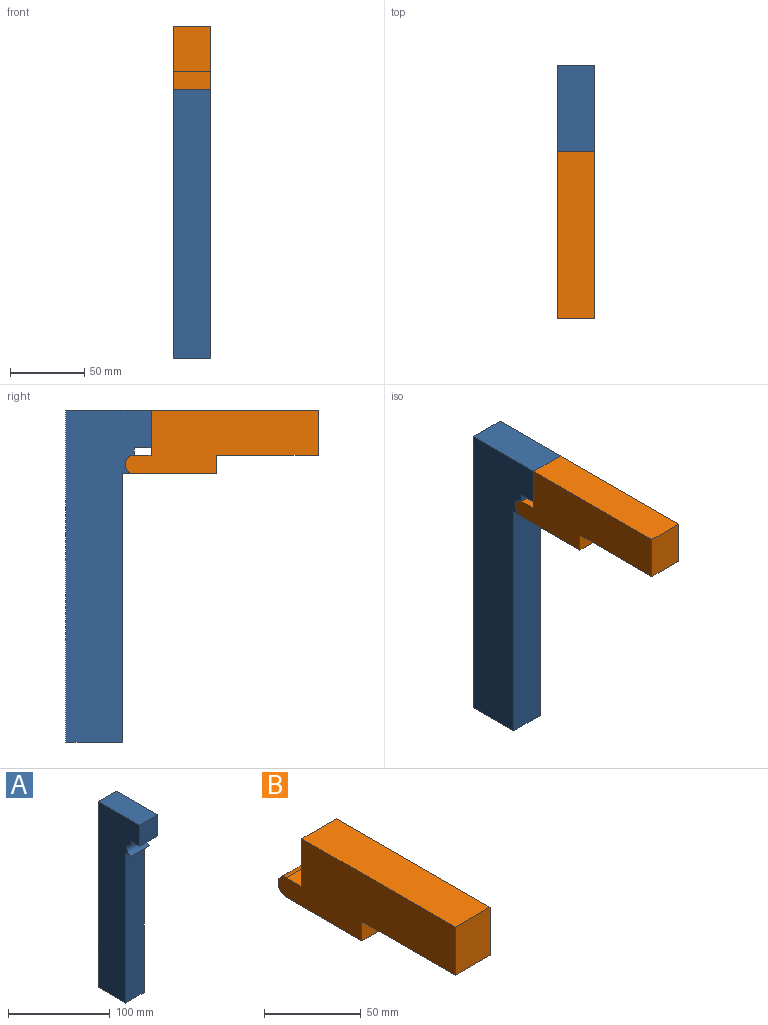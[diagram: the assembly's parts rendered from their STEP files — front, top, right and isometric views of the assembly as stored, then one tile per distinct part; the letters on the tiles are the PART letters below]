
ASSEMBLY  parts=2 mates=1
PART A: 11 faces, bbox 25.4x57.3x223 mm
  f0: plane 25.4x11.35mm, normal (0,0,-1), area 288.3mm2, adj f1,f8,f9,f10
  f1: plane 25.4x5.08mm, normal (0,-1,0), area 129mm2, adj f0,f2,f9,f10
  f2: cylinder r=6.14mm len=25.4mm, axis (-1,0,0), area 490.1mm2, adj f1,f3,f9,f10
  f3: plane 25.4x7.7mm, normal (0,0,-1), area 195.6mm2, adj f2,f4,f9,f10
  f4: plane 180.26x25.4mm, normal (0,-1,0), area 4578.6mm2, adj f3,f5,f9,f10
  f5: plane 38.21x25.4mm, normal (0,0,-1), area 970.4mm2, adj f4,f6,f9,f10
  f6: plane 223.02x25.4mm, normal (0,1,0), area 5664.8mm2, adj f5,f7,f9,f10
  f7: plane 57.26x25.4mm, normal (0,0,1), area 1454.3mm2, adj f6,f8,f9,f10
  f8: plane 25.4x25.4mm, normal (0,-1,0), area 645.2mm2, adj f0,f7,f9,f10
  f9: plane 223.02x57.26mm, normal (1,0,0), area 9078.9mm2, adj f0,f1,f2,f3,f4,f5,f6,f7
  f10: plane 223.02x57.26mm, normal (-1,0,0), area 9078.9mm2, adj f0,f1,f2,f3,f4,f5,f6,f7
PART B: 10 faces, bbox 25.4x129.7x42.8 mm
  f0: plane 68.31x25.4mm, normal (0,0,-1), area 1735.2mm2, adj f1,f7,f8,f9
  f1: plane 25.4x12.28mm, normal (0,-1,0), area 312mm2, adj f0,f2,f8,f9
  f2: plane 55.28x25.4mm, normal (0,0,-1), area 1404mm2, adj f1,f3,f8,f9
  f3: cylinder r=6.14mm len=25.4mm, axis (-1,0,0), area 490.1mm2, adj f2,f4,f8,f9
  f4: plane 25.4x11.35mm, normal (0,0,1), area 288.3mm2, adj f3,f5,f8,f9
  f5: plane 30.48x25.4mm, normal (0,1,0), area 774.2mm2, adj f4,f6,f8,f9
  f6: plane 112.24x25.4mm, normal (0,0,1), area 2850.9mm2, adj f5,f7,f8,f9
  f7: plane 30.48x25.4mm, normal (0,-1,0), area 774.2mm2, adj f0,f6,f8,f9
  f8: plane 129.73x42.76mm, normal (1,0,0), area 4159.3mm2, adj f0,f1,f2,f3,f4,f5,f6,f7
  f9: plane 129.73x42.76mm, normal (-1,0,0), area 4159.3mm2, adj f0,f1,f2,f3,f4,f5,f6,f7
PLACE A at identity fixed
PLACE B at identity
MATE revolute B.f3 <-> A.f2  axis (1,0,0) through (25.4,-7.7,186.4)mm
